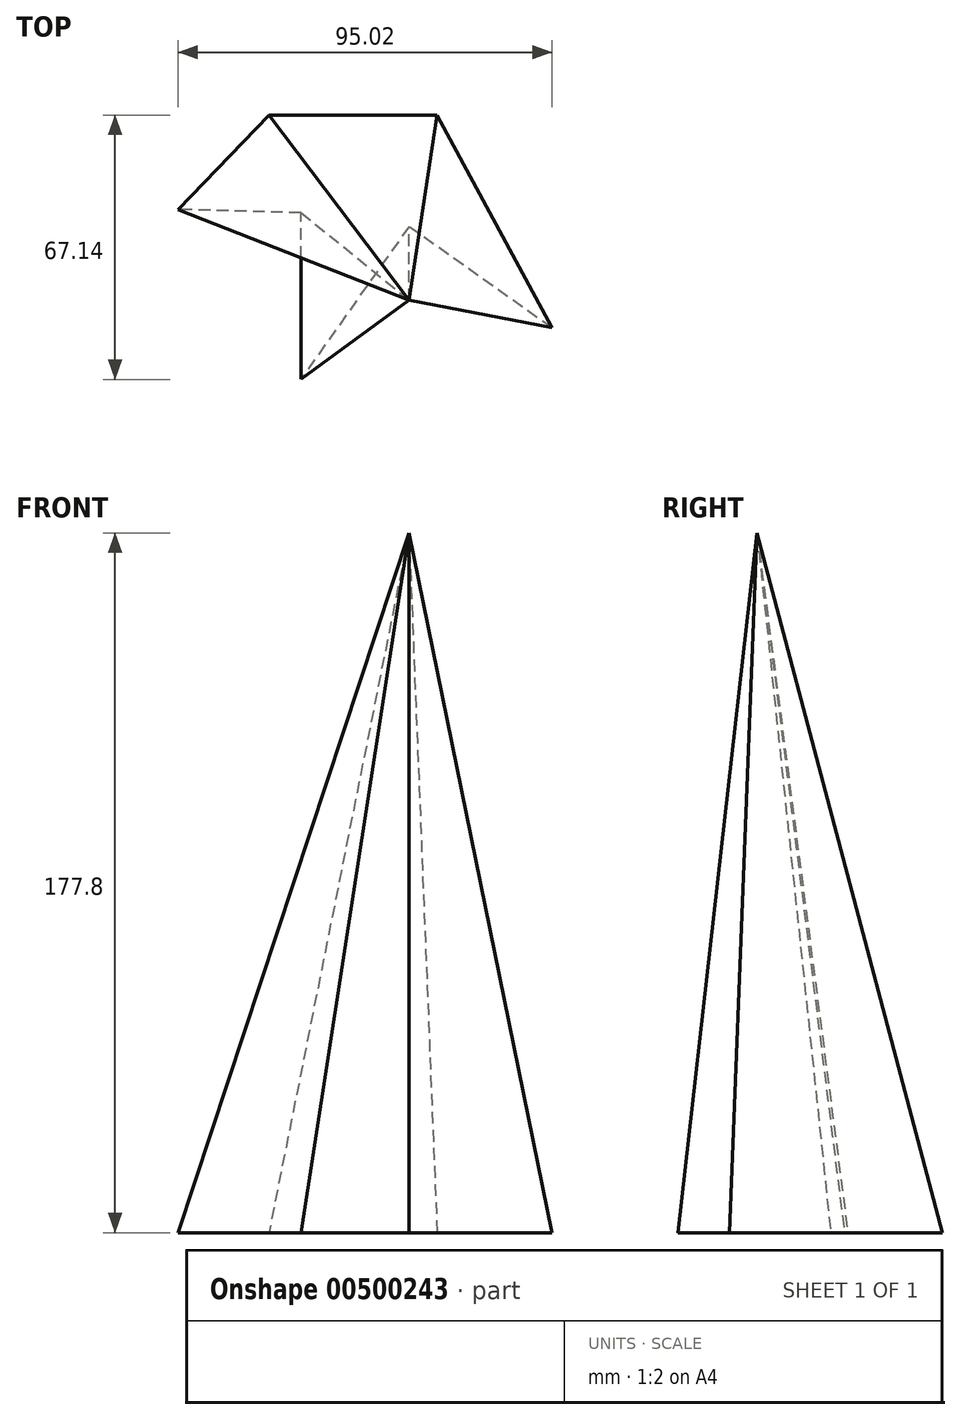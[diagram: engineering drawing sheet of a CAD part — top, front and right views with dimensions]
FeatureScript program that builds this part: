
annotation { "Feature Type Name" : "Feature", "Feature Type Description" : "" }
export const myFeature = defineFeature(function(context is Context, id is Id, definition is map)
    precondition{}
    {
        {
            var Q0;
            Q0=qCreatedBy(makeId("Top.planeOp"),FACE);
            var sketch = newSketch(context, id + "F0", { "sketchPlane" : qUnion([Q0])});
            skLineSegment(sketch, "E0", {"start": v(-58.67, 23.09) * mm, "end": v(-35.57, 47.06) * mm});
            skLineSegment(sketch, "E1", {"start": v(-35.57, 47.06) * mm, "end": v(7.15, 47.06) * mm});
            skLineSegment(sketch, "E2", {"start": v(7.15, 47.06) * mm, "end": v(36.35, -6.99) * mm});
            skLineSegment(sketch, "E3", {"start": v(36.35, -6.99) * mm, "end": v(0, 18.73) * mm});
            skLineSegment(sketch, "E4", {"start": v(0, 18.73) * mm, "end": v(-27.45, -20.08) * mm});
            skLineSegment(sketch, "E5", {"start": v(-27.45, -20.08) * mm, "end": v(-27.45, 22.22) * mm});
            skLineSegment(sketch, "E6", {"start": v(-27.45, 22.22) * mm, "end": v(-58.67, 23.09) * mm});
            skSolve(sketch);
        }
        {
            var Q0;
            Q0=qCreatedBy(makeId("Top.planeOp"),FACE);
            cPlane(context, id + "F1", {"entities" : qUnion([Q0]), "cplaneType" : CPlaneType.OFFSET, "offset" : 177.8 * mm, "width" : 150 * mm, "height" : 150 * mm});
        }
        {
            var Q0;
            Q0=qCreatedBy(id+"F1.planeOp",FACE);
            var sketch = newSketch(context, id + "F2", { "sketchPlane" : qUnion([Q0])});
            skPoint(sketch, "E7", {"position": v(0, 0) * mm});
            skSolve(sketch);
        }
        {
            var Q0;
            Q0=sQuery(id+"F2.wireOp",VERTEX,"E7");
            var Q1;
            Q1=makeQuery(id+"F0.imprint","IMPRINT",FACE,{"disambiguationData":[TD([[makeQuery(id+"F0.imprint","IMPRINT",EDGE,{"derivedFrom":sQuery(id+"F0.wireOp",EDGE,"E0")}),-1.0]])]});
            loft(context, id + "F3", {"sheetProfilesArray" : [{ "sheetProfileEntities" : qUnion([Q0]) }, { "sheetProfileEntities" : qUnion([Q1]) }]});
        }
    });
